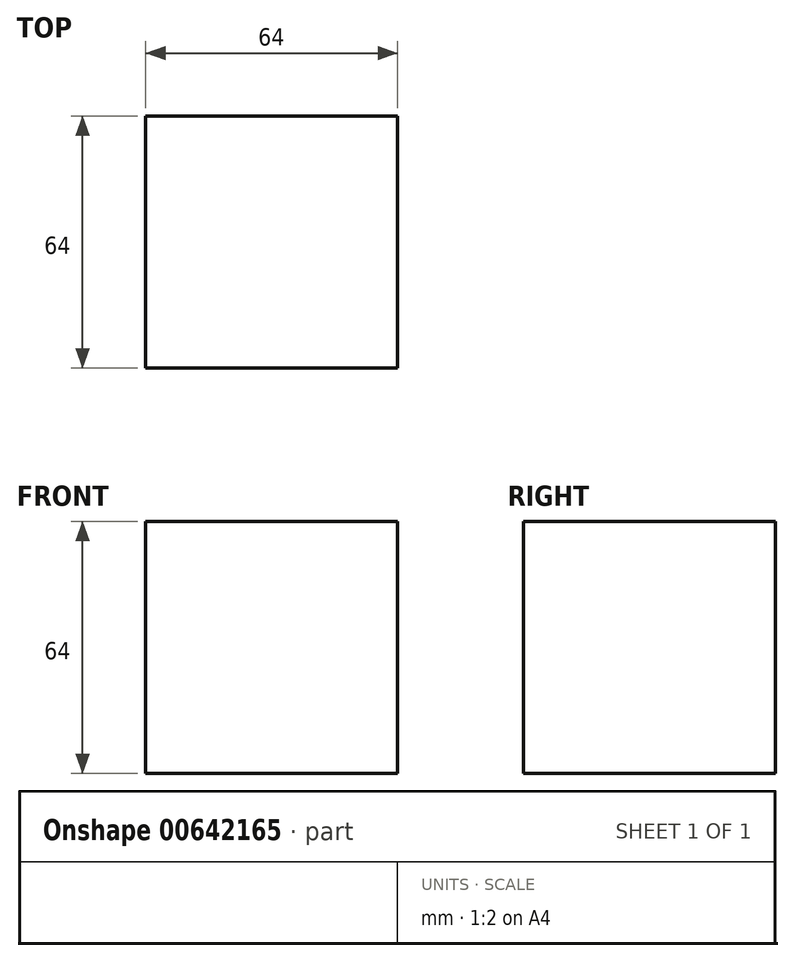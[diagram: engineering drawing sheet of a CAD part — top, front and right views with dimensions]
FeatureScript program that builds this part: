
annotation { "Feature Type Name" : "Feature", "Feature Type Description" : "" }
export const myFeature = defineFeature(function(context is Context, id is Id, definition is map)
    precondition{}
    {
        {
            var Q0;
            Q0=qCreatedBy(makeId("Top.planeOp"),FACE);
            var sketch = newSketch(context, id + "F0", { "sketchPlane" : qUnion([Q0])});
            skLineSegment(sketch, "E0.bottom", {"start": v(-11.52, 26.12) * mm, "end": v(52.48, 26.12) * mm});
            skLineSegment(sketch, "E0.top", {"start": v(-11.52, -37.88) * mm, "end": v(52.48, -37.88) * mm});
            skLineSegment(sketch, "E0.left", {"start": v(-11.52, 26.12) * mm, "end": v(-11.52, -37.88) * mm});
            skLineSegment(sketch, "E0.right", {"start": v(52.48, 26.12) * mm, "end": v(52.48, -37.88) * mm});
            skSolve(sketch);
        }
        {
            var Q0;
            Q0=makeQuery(id+"F0.imprint","IMPRINT",FACE,{"disambiguationData":[TD([[makeQuery(id+"F0.imprint","IMPRINT",EDGE,{"derivedFrom":sQuery(id+"F0.wireOp",EDGE,"E0.bottom")}),-1.0]])]});
            extrude(context, id + "F1", {"entities" : qUnion([Q0]), "depth" : 64 * mm, "offsetDistance" : 25 * mm});
        }
    });
